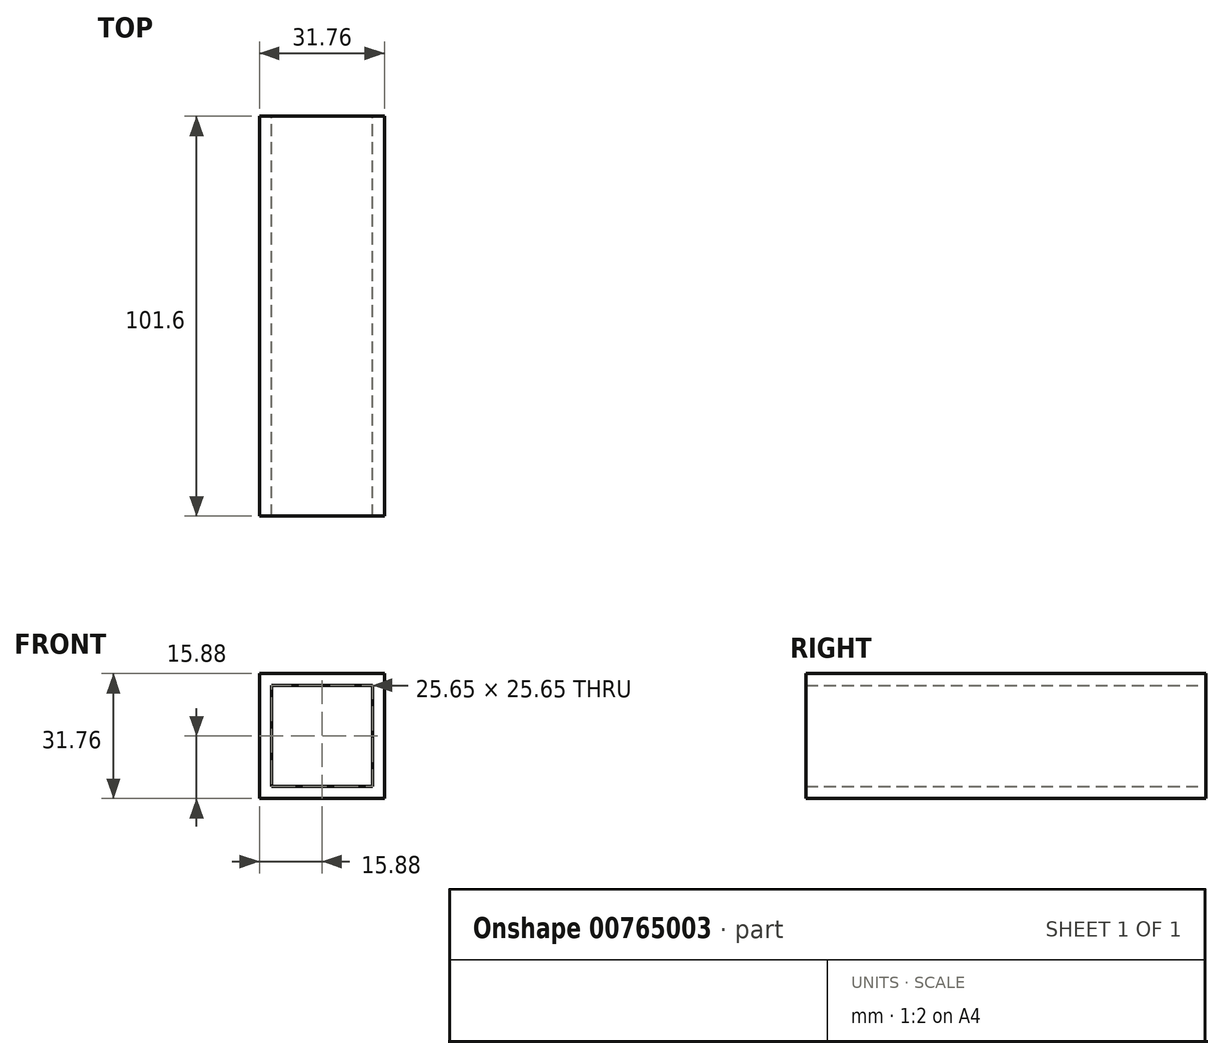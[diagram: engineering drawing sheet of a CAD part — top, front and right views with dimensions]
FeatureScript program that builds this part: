
annotation { "Feature Type Name" : "Feature", "Feature Type Description" : "" }
export const myFeature = defineFeature(function(context is Context, id is Id, definition is map)
    precondition{}
    {
        {
            var Q0;
            Q0=qCreatedBy(makeId("Front.planeOp"),FACE);
            var sketch = newSketch(context, id + "F0", { "sketchPlane" : qUnion([Q0])});
            skLineSegment(sketch, "E0.bottom", {"start": v(15.88, 15.88) * mm, "end": v(-15.88, 15.88) * mm});
            skLineSegment(sketch, "E0.top", {"start": v(15.88, -15.88) * mm, "end": v(-15.88, -15.88) * mm});
            skLineSegment(sketch, "E0.left", {"start": v(15.88, 15.88) * mm, "end": v(15.88, -15.88) * mm});
            skLineSegment(sketch, "E0.right", {"start": v(-15.88, 15.88) * mm, "end": v(-15.88, -15.88) * mm});
            skPoint(sketch, "E0.middle", {"position": v(0, 0) * mm});
            skLineSegment(sketch, "E1.0", {"start": v(-12.83, 12.83) * mm, "end": v(-12.83, -12.83) * mm});
            skLineSegment(sketch, "E1.1", {"start": v(12.83, 12.83) * mm, "end": v(-12.83, 12.83) * mm});
            skLineSegment(sketch, "E1.2", {"start": v(12.83, 12.83) * mm, "end": v(12.83, -12.83) * mm});
            skLineSegment(sketch, "E1.3", {"start": v(12.83, -12.83) * mm, "end": v(-12.83, -12.83) * mm});
            skSolve(sketch);
        }
        {
            var Q0;
            Q0 = qSketchRegion(id + "F0", true);
            extrude(context, id + "F1", {"entities" : qUnion([Q0]), "depth" : 101.6 * mm, "offsetDistance" : 25.4 * mm});
        }
    });
